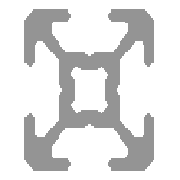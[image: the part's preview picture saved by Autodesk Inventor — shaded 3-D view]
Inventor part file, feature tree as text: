
AUTODESK INVENTOR PART (.ipt)
format: ipt  version: 2015 (Build 190159000, 159)  size: 385,024 bytes
history: native  units: mm
features: other x3, extrude x1, sketch x1
ambient origin geometry x8: Origin, YZ Plane, XZ Plane, XY Plane, X Axis, Y Axis, Z Axis, Center Point
bodies: Body1 (feature_tree)
feature tree (5):
  other  "Blocks"
  extrude  "Extrusion3"  [1 undecoded]
  sketch  "Sketch1"  dims[d23=0.0mm]
  other  "20x20"
  other  "20x20:1"
note: 1 required parameter value undecoded (feature->parameter linkage not recoverable at this tier; creation-order binding heuristic only, values carry confidence <= 0.55)
